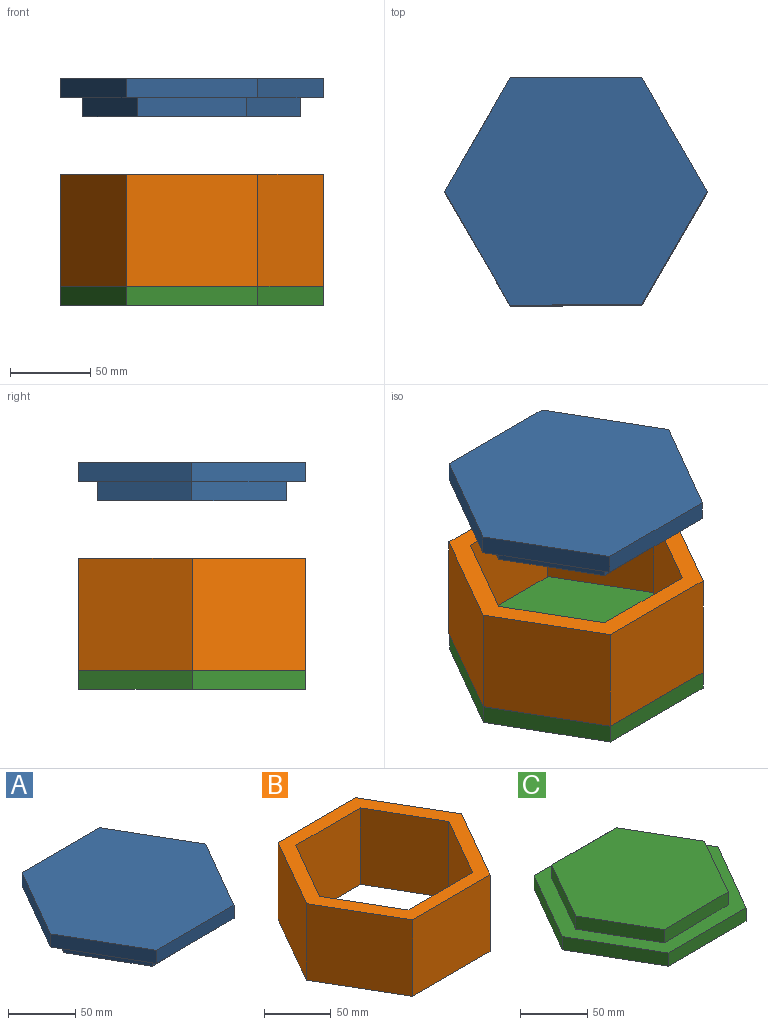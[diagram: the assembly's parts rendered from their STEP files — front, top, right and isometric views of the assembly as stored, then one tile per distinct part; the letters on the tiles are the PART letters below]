
ASSEMBLY  parts=3 mates=2
PART A: 15 faces, bbox 163.9x141.8x24 mm
  f0: plane 68.26x12mm, normal (0.01,-1,0), area 819.1mm2, adj f1,f5,f6,f13
  f1: plane 58.66x33.72mm, normal (0.87,-0.5,0), area 811.9mm2, adj f0,f2,f6,f13
  f2: plane 58.76x34.13mm, normal (0.86,0.5,0), area 815.4mm2, adj f1,f3,f6,f13
  f3: plane 68.01x12mm, normal (0,1,0), area 816.2mm2, adj f2,f4,f6,f13
  f4: plane 58.92x33.97mm, normal (-0.87,0.5,0), area 816.1mm2, adj f3,f5,f6,f13
  f5: plane 59.26x34.13mm, normal (-0.87,-0.5,0), area 820.6mm2, adj f0,f4,f6,f13
  f6: plane 136.11x118.25mm, normal (0,0,-1), area 12030mm2, adj f0,f1,f2,f3,f4,f5
  f7: plane 70.85x41.05mm, normal (-0.87,0.5,0), area 982.5mm2, adj f8,f12,f13,f14
  f8: plane 70.96x40.87mm, normal (-0.87,-0.5,0), area 982.7mm2, adj f7,f9,f13,f14
  f9: plane 82.09x12mm, normal (0,-1,0), area 985.1mm2, adj f8,f10,f13,f14
  f10: plane 70.73x40.98mm, normal (0.87,-0.5,0), area 980.9mm2, adj f9,f11,f13,f14
  f11: plane 70.85x40.9mm, normal (0.87,0.5,0), area 981.7mm2, adj f10,f12,f13,f14
  f12: plane 82x12mm, normal (0,1,0), area 984mm2, adj f7,f11,f13,f14
  f13: plane 163.95x141.81mm, normal (0,0,-1), area 5397.5mm2, adj f0,f1,f2,f3,f4,f5,f7,f8
  f14: plane 163.95x141.81mm, normal (0,0,1), area 17427.5mm2, adj f7,f8,f9,f10,f11,f12
PART B: 14 faces, bbox 164x142.2x70 mm
  f0: plane 82x70mm, normal (0,1,0), area 5740mm2, adj f1,f11,f12,f13
  f1: plane 71.12x70mm, normal (-0.87,0.5,0), area 5740mm2, adj f0,f2,f12,f13
  f2: plane 70.9x70mm, normal (-0.86,-0.5,0), area 5740mm2, adj f1,f3,f12,f13
  f3: plane 82x70mm, normal (0,-1,0), area 5740mm2, adj f2,f4,f12,f13
  f4: plane 71.12x70mm, normal (0.87,-0.5,0), area 5740mm2, adj f3,f11,f12,f13
  f5: plane 70x68.44mm, normal (0,-1,0), area 4791.1mm2, adj f6,f10,f12,f13
  f6: plane 70x59.25mm, normal (-0.87,-0.5,0), area 4791.1mm2, adj f5,f7,f12,f13
  f7: plane 70x59.3mm, normal (-0.87,0.5,0), area 4791.1mm2, adj f6,f8,f12,f13
  f8: plane 70x68.44mm, normal (0,1,0), area 4791.1mm2, adj f7,f9,f12,f13
  f9: plane 70x59.25mm, normal (0.87,0.5,0), area 4791.1mm2, adj f8,f10,f12,f13
  f10: plane 70x59.3mm, normal (0.87,-0.5,0), area 4791.1mm2, adj f5,f9,f12,f13
  f11: plane 70.9x70mm, normal (0.86,0.5,0), area 5740mm2, adj f0,f4,f12,f13
  f12: plane 164x142.25mm, normal (0,0,1), area 5298.3mm2, adj f0,f1,f2,f3,f4,f5,f6,f7
  f13: plane 164x142.25mm, normal (0,0,-1), area 5298.3mm2, adj f0,f1,f2,f3,f4,f5,f6,f7
PART C: 15 faces, bbox 163.9x141.8x24 mm
  f0: plane 68.26x12mm, normal (0.01,-1,0), area 819.1mm2, adj f1,f5,f6,f13
  f1: plane 58.66x33.72mm, normal (0.87,-0.5,0), area 811.9mm2, adj f0,f2,f6,f13
  f2: plane 58.76x34.13mm, normal (0.86,0.5,0), area 815.4mm2, adj f1,f3,f6,f13
  f3: plane 68.01x12mm, normal (0,1,0), area 816.2mm2, adj f2,f4,f6,f13
  f4: plane 58.92x33.97mm, normal (-0.87,0.5,0), area 816.1mm2, adj f3,f5,f6,f13
  f5: plane 59.26x34.13mm, normal (-0.87,-0.5,0), area 820.6mm2, adj f0,f4,f6,f13
  f6: plane 136.11x118.25mm, normal (0,0,1), area 12030mm2, adj f0,f1,f2,f3,f4,f5
  f7: plane 70.85x41.05mm, normal (-0.87,0.5,0), area 982.5mm2, adj f8,f12,f13,f14
  f8: plane 70.96x40.87mm, normal (-0.87,-0.5,0), area 982.7mm2, adj f7,f9,f13,f14
  f9: plane 82.09x12mm, normal (0,-1,0), area 985.1mm2, adj f8,f10,f13,f14
  f10: plane 70.73x40.98mm, normal (0.87,-0.5,0), area 980.9mm2, adj f9,f11,f13,f14
  f11: plane 70.85x40.9mm, normal (0.87,0.5,0), area 981.7mm2, adj f10,f12,f13,f14
  f12: plane 82x12mm, normal (0,1,0), area 984mm2, adj f7,f11,f13,f14
  f13: plane 163.95x141.81mm, normal (0,0,1), area 5397.5mm2, adj f0,f1,f2,f3,f4,f5,f7,f8
  f14: plane 163.95x141.81mm, normal (0,0,-1), area 17427.5mm2, adj f7,f8,f9,f10,f11,f12
PLACE A rot(axis=(0,0,1),0deg) t=(182.44,-42.02,265.87)mm
PLACE B rot(axis=(0,0,1),0deg) t=(-5.26,69.29,136.26)mm
PLACE C rot(axis=(0,0,1),0deg) t=(-59.29,-85.75,124.26)mm
MATE fastened C.f13 <-> B.f13  axis (0,0,1) through (35.93,-1.61,136.26)mm
MATE slider A.f13 <-> B.f12  axis (0,0,-1) through (76.74,69.52,253.87)mm
